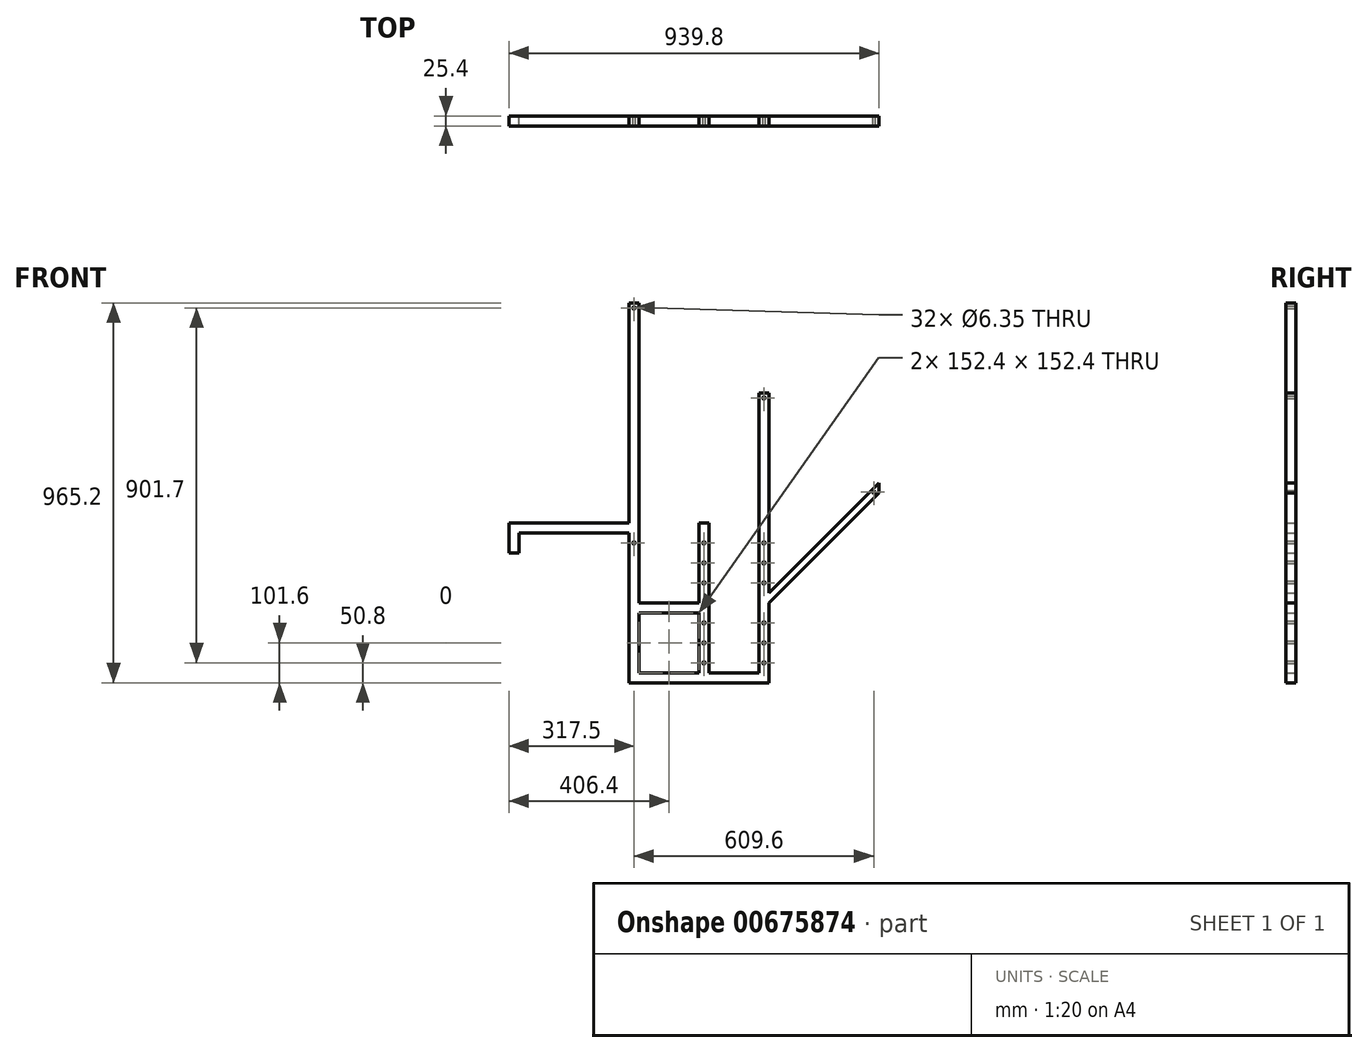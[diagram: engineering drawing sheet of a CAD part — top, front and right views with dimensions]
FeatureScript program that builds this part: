
annotation { "Feature Type Name" : "Feature", "Feature Type Description" : "" }
export const myFeature = defineFeature(function(context is Context, id is Id, definition is map)
    precondition{}
    {
        {
            var Q0;
            Q0=qCreatedBy(makeId("Front.planeOp"),FACE);
            var sketch = newSketch(context, id + "F0", { "sketchPlane" : qUnion([Q0])});
            skLineSegment(sketch, "E0.bottom", {"start": v(0, 0) * mm, "end": v(279.4, 0) * mm});
            skLineSegment(sketch, "E0.top", {"start": v(0, -25.4) * mm, "end": v(279.4, -25.4) * mm});
            skLineSegment(sketch, "E0.left", {"start": v(0, 0) * mm, "end": v(0, -25.4) * mm});
            skLineSegment(sketch, "E0.right", {"start": v(279.4, 0) * mm, "end": v(279.4, -25.4) * mm});
            skLineSegment(sketch, "E1.bottom", {"start": v(0, 0) * mm, "end": v(-25.4, 0) * mm});
            skLineSegment(sketch, "E1.top", {"start": v(0, -76.2) * mm, "end": v(-25.4, -76.2) * mm});
            skLineSegment(sketch, "E1.left", {"start": v(0, 0) * mm, "end": v(0, -76.2) * mm});
            skLineSegment(sketch, "E1.right", {"start": v(-25.4, 0) * mm, "end": v(-25.4, -76.2) * mm});
            skLineSegment(sketch, "E2.bottom", {"start": v(279.4, 0) * mm, "end": v(304.8, 0) * mm});
            skLineSegment(sketch, "E2.top", {"start": v(279.4, -406.4) * mm, "end": v(304.8, -406.4) * mm});
            skLineSegment(sketch, "E2.left", {"start": v(279.4, 0) * mm, "end": v(279.4, -406.4) * mm});
            skLineSegment(sketch, "E2.right", {"start": v(304.8, 0) * mm, "end": v(304.8, -406.4) * mm});
            skLineSegment(sketch, "E3.bottom", {"start": v(304.8, -203.2) * mm, "end": v(457.2, -203.2) * mm});
            skLineSegment(sketch, "E3.top", {"start": v(304.8, -228.6) * mm, "end": v(457.2, -228.6) * mm});
            skLineSegment(sketch, "E3.left", {"start": v(304.8, -203.2) * mm, "end": v(304.8, -228.6) * mm});
            skLineSegment(sketch, "E3.right", {"start": v(457.2, -203.2) * mm, "end": v(457.2, -228.6) * mm});
            skLineSegment(sketch, "E4.bottom", {"start": v(304.8, -406.4) * mm, "end": v(609.6, -406.4) * mm});
            skLineSegment(sketch, "E4.top", {"start": v(304.8, -381) * mm, "end": v(609.6, -381) * mm});
            skLineSegment(sketch, "E4.left", {"start": v(304.8, -406.4) * mm, "end": v(304.8, -381) * mm});
            skLineSegment(sketch, "E4.right", {"start": v(609.6, -406.4) * mm, "end": v(609.6, -381) * mm});
            skLineSegment(sketch, "E5.bottom", {"start": v(457.2, -406.4) * mm, "end": v(482.6, -406.4) * mm});
            skLineSegment(sketch, "E5.top", {"start": v(457.2, 0) * mm, "end": v(482.6, 0) * mm});
            skLineSegment(sketch, "E5.left", {"start": v(457.2, -406.4) * mm, "end": v(457.2, 0) * mm});
            skLineSegment(sketch, "E5.right", {"start": v(482.6, -406.4) * mm, "end": v(482.6, 0) * mm});
            skPoint(sketch, "E6.oppositeSnap0", {"position": v(482.6, -203.2) * mm});
            skLineSegment(sketch, "E6.bottom", {"start": v(609.6, -406.4) * mm, "end": v(635, -406.4) * mm});
            skLineSegment(sketch, "E6.top", {"start": v(609.6, -203.2) * mm, "end": v(635, -203.2) * mm});
            skLineSegment(sketch, "E6.left", {"start": v(609.6, -406.4) * mm, "end": v(609.6, -203.2) * mm});
            skLineSegment(sketch, "E6.right", {"start": v(635, -406.4) * mm, "end": v(635, -203.2) * mm});
            skLineSegment(sketch, "E7.top", {"start": v(279.4, 558.8) * mm, "end": v(304.8, 558.8) * mm});
            skLineSegment(sketch, "E7.left", {"start": v(279.4, 0) * mm, "end": v(279.4, 558.8) * mm});
            skLineSegment(sketch, "E7.right", {"start": v(304.8, 0) * mm, "end": v(304.8, 558.8) * mm});
            skLineSegment(sketch, "E8.top", {"start": v(609.6, 330.2) * mm, "end": v(635, 330.2) * mm});
            skLineSegment(sketch, "E8.left", {"start": v(609.6, -203.2) * mm, "end": v(609.6, 330.2) * mm});
            skLineSegment(sketch, "E8.right", {"start": v(635, -203.2) * mm, "end": v(635, 330.2) * mm});
            skLineSegment(sketch, "E9", {"start": v(609.6, -203.2) * mm, "end": v(914.4, -203.2) * mm, "construction": true});
            skLineSegment(sketch, "E10", {"start": v(914.4, -203.2) * mm, "end": v(914.4, 324.73) * mm, "construction": true});
            skLineSegment(sketch, "E11", {"start": v(609.6, -203.2) * mm, "end": v(914.4, 101.6) * mm});
            skLineSegment(sketch, "E12", {"start": v(635, -203.2) * mm, "end": v(914.4, 76.2) * mm});
            skLineSegment(sketch, "E13", {"start": v(914.4, 101.6) * mm, "end": v(914.4, 76.2) * mm});
            skSolve(sketch);
        }
        {
            var Q0;
            Q0 = qSketchRegion(id + "F0", true);
            extrude(context, id + "F1", {"entities" : qUnion([Q0]), "endBound" : BoundingType.SYMMETRIC, "depth" : 25.4 * mm, "offsetDistance" : 25.4 * mm});
        }
        {
            var Q0;
            Q0=makeQuery(id+"F1.opExtrude","CAP_FACE",FACE,{"disambiguationData":[OSD([sQuery(id+"F0.wireOp",EDGE,"E0.bottom"),sQuery(id+"F0.wireOp",EDGE,"E0.top"),sQuery(id+"F0.wireOp",EDGE,"E1.bottom"),sQuery(id+"F0.wireOp",EDGE,"E1.top"),sQuery(id+"F0.wireOp",EDGE,"E1.left"),sQuery(id+"F0.wireOp",EDGE,"E1.right"),sQuery(id+"F0.wireOp",EDGE,"E2.top"),sQuery(id+"F0.wireOp",EDGE,"E2.left"),sQuery(id+"F0.wireOp",EDGE,"E2.right"),sQuery(id+"F0.wireOp",EDGE,"E3.bottom"),sQuery(id+"F0.wireOp",EDGE,"E3.top"),sQuery(id+"F0.wireOp",EDGE,"E4.bottom"),sQuery(id+"F0.wireOp",EDGE,"E4.top"),sQuery(id+"F0.wireOp",EDGE,"E5.bottom"),sQuery(id+"F0.wireOp",EDGE,"E5.top"),sQuery(id+"F0.wireOp",EDGE,"E5.left"),sQuery(id+"F0.wireOp",EDGE,"E5.right"),sQuery(id+"F0.wireOp",EDGE,"E6.bottom"),sQuery(id+"F0.wireOp",EDGE,"E6.left"),sQuery(id+"F0.wireOp",EDGE,"E6.right"),sQuery(id+"F0.wireOp",EDGE,"E7.top"),sQuery(id+"F0.wireOp",EDGE,"E7.left"),sQuery(id+"F0.wireOp",EDGE,"E7.right"),sQuery(id+"F0.wireOp",EDGE,"E8.top"),sQuery(id+"F0.wireOp",EDGE,"E8.left"),sQuery(id+"F0.wireOp",EDGE,"E8.right"),sQuery(id+"F0.wireOp",EDGE,"E11"),sQuery(id+"F0.wireOp",EDGE,"E12"),sQuery(id+"F0.wireOp",EDGE,"E13")])],"isStart":false});
            var sketch = newSketch(context, id + "F2", { "sketchPlane" : qUnion([Q0])});
            skCircle(sketch, "E14", {"center": v(469.9, -101.6) * mm, "radius": 3.17 * mm});
            skCircle(sketch, "E15", {"center": v(469.9, -50.8) * mm, "radius": 3.18 * mm});
            skCircle(sketch, "E16", {"center": v(469.9, -152.4) * mm, "radius": 3.18 * mm});
            skCircle(sketch, "E17", {"center": v(469.9, -304.8) * mm, "radius": 3.17 * mm});
            skCircle(sketch, "E18", {"center": v(469.9, -254) * mm, "radius": 3.18 * mm});
            skCircle(sketch, "E19", {"center": v(469.9, -355.6) * mm, "radius": 3.18 * mm});
            skCircle(sketch, "E20", {"center": v(622.3, -101.6) * mm, "radius": 3.18 * mm});
            skCircle(sketch, "E21", {"center": v(622.3, -50.8) * mm, "radius": 3.18 * mm});
            skCircle(sketch, "E22", {"center": v(622.3, -152.4) * mm, "radius": 3.18 * mm});
            skCircle(sketch, "E23", {"center": v(622.3, -254) * mm, "radius": 3.18 * mm});
            skCircle(sketch, "E24", {"center": v(622.3, -304.8) * mm, "radius": 3.18 * mm});
            skCircle(sketch, "E25", {"center": v(622.3, -355.6) * mm, "radius": 3.18 * mm});
            skCircle(sketch, "E26", {"center": v(292.1, -50.8) * mm, "radius": 3.17 * mm});
            skCircle(sketch, "E27", {"center": v(292.1, 546.1) * mm, "radius": 3.17 * mm});
            skCircle(sketch, "E28", {"center": v(622.3, 317.5) * mm, "radius": 3.17 * mm});
            skCircle(sketch, "E29", {"center": v(901.7, 78.12) * mm, "radius": 3.17 * mm});
            skSolve(sketch);
        }
        {
            var Q0;
            Q0 = qSketchRegion(id + "F2", true);
            extrude(context, id + "F3", {"entities" : qUnion([Q0]), "operationType" : NewBodyOperationType.REMOVE, "oppositeDirection" : true, "depth" : 25.4 * mm, "offsetDistance" : 25.4 * mm});
        }
    });
